# Revit family: Arper_Aava-02_trestle-swivel_wood_front-face-upholstery_7635
name_source: partatom
category: Furniture
units: mm (PartAtom-declared; Revit-internal decimal feet)

## family parameters
Always vertical = Yes
Cut with Voids When Loaded = No
OmniClass Number = 23.40.20.00
OmniClass Title = General Furniture and Specialties
Room Calculation Point = No
Shared = No
Work Plane-Based = No

## types (1)
- Arper_Aava-02_trestle-swivel_wood_front-face-upholstery_7635
    Default Elevation = 0 mm  [stored 0 ft]
    Description = Chair on a swivel trestle base in powder-coated aluminium. Shell in 
plywood with a reconstituted oak or walnut finish, with front 
upholstery in fabric, leather, coated fabric or customer’s own 
material. Optional armrests in the same colour as the base are also 
available, equipped with pads in wood in the same finish of the shell. 
Glides are also available, with felt insert for wood floors.
    Manufacturer = ARPER s.p.a.
    Model = Aava 02
    URL = http://www.arper.com

note: [stored X ft] marks values corroborated as IEEE doubles in the binary element streams (Revit-internal decimal feet)
